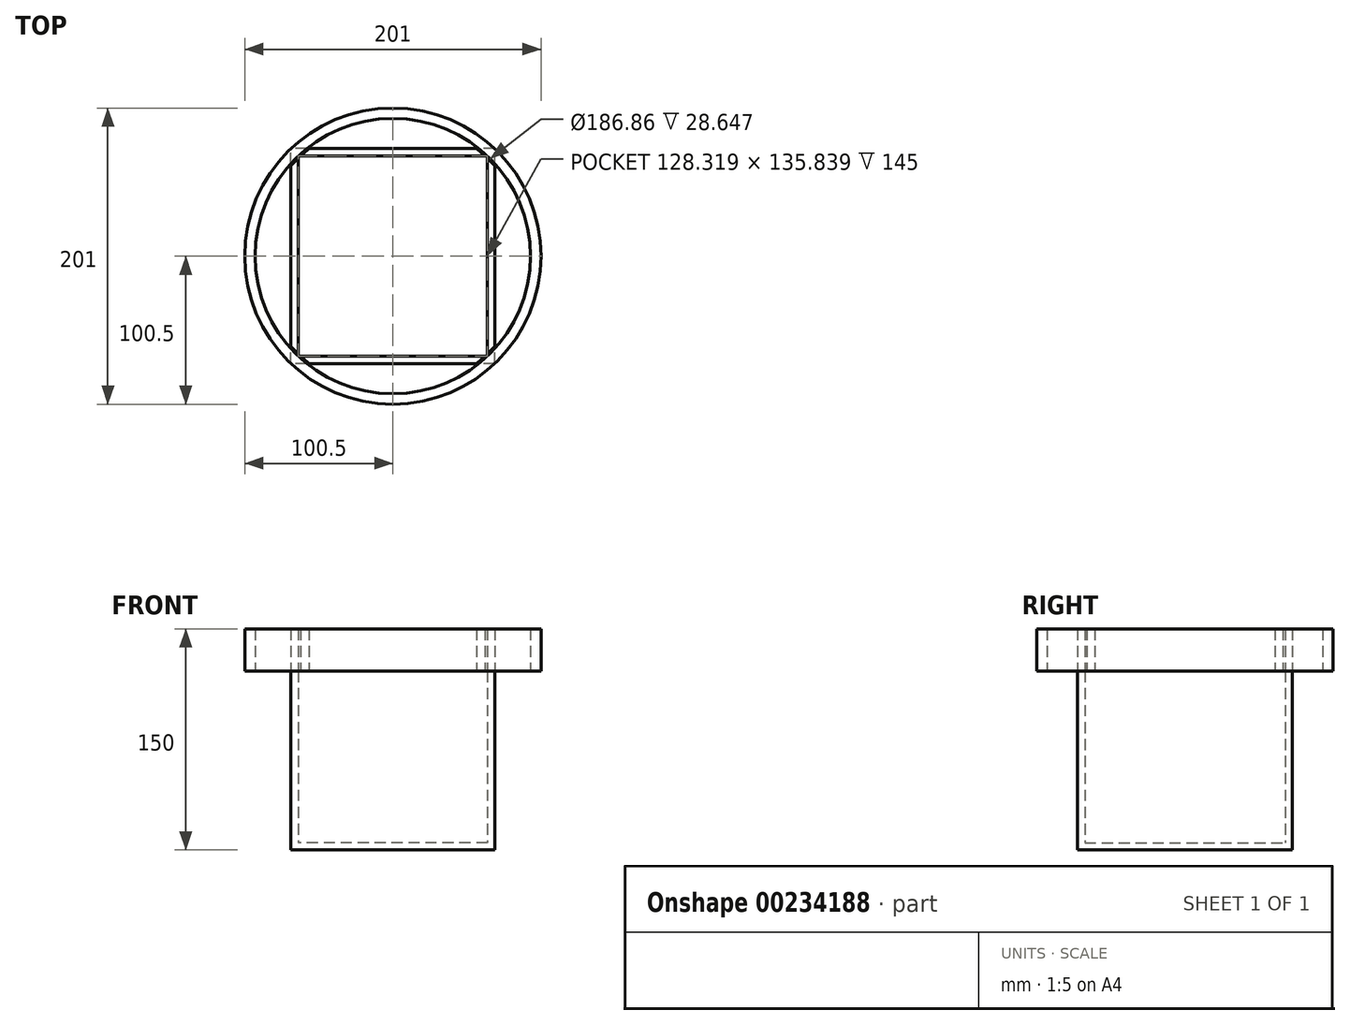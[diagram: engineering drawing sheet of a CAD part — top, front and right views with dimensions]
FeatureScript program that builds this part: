
annotation { "Feature Type Name" : "Feature", "Feature Type Description" : "" }
export const myFeature = defineFeature(function(context is Context, id is Id, definition is map)
    precondition{}
    {
        {
            assignVariable(context, id + "F0", {"name" : "height", "anyValue" : 150});
        }
        {
            assignVariable(context, id + "F1", {"name" : "thickness", "anyValue" : 5});
        }
        {
            assignVariable(context, id + "F2", {"name" : "proportion", "anyValue" : 1 - (1 - 1 / 1.62) / 2});
        }
        {
            var Q0;
            Q0=qCreatedBy(makeId("Top.planeOp"),FACE);
            var sketch = newSketch(context, id + "F3", { "sketchPlane" : qUnion([Q0])});
            skLineSegment(sketch, "E0.bottom", {"start": v(69.16, -72.92) * mm, "end": v(-69.16, -72.92) * mm});
            skLineSegment(sketch, "E0.top", {"start": v(69.16, 72.92) * mm, "end": v(-69.16, 72.92) * mm});
            skLineSegment(sketch, "E0.left", {"start": v(69.16, -72.92) * mm, "end": v(69.16, 72.92) * mm});
            skLineSegment(sketch, "E0.right", {"start": v(-69.16, -72.92) * mm, "end": v(-69.16, 72.92) * mm});
            skPoint(sketch, "E0.middle", {"position": v(0, 0) * mm});
            skCircle(sketch, "E1", {"center": v(0, 0) * mm, "radius": 100.5 * mm, "construction": true});
            skCircle(sketch, "E2", {"center": v(0, 0) * mm, "radius": 93.43 * mm, "construction": true});
            skLineSegment(sketch, "E3.bottom", {"start": v(64.16, -67.92) * mm, "end": v(-64.16, -67.92) * mm});
            skLineSegment(sketch, "E3.top", {"start": v(64.16, 67.92) * mm, "end": v(-64.16, 67.92) * mm});
            skLineSegment(sketch, "E3.left", {"start": v(64.16, -67.92) * mm, "end": v(64.16, 67.92) * mm});
            skLineSegment(sketch, "E3.right", {"start": v(-64.16, -67.92) * mm, "end": v(-64.16, 67.92) * mm});
            skSolve(sketch);
        }
        {
            var Q0;
            Q0=makeQuery(id+"F3.imprint","IMPRINT",FACE,{"disambiguationData":[TD([[makeQuery(id+"F3.imprint","IMPRINT",EDGE,{"derivedFrom":sQuery(id+"F3.wireOp",EDGE,"E3.bottom")}),-1.0]])]});
            extrude(context, id + "F4", {"entities" : qUnion([Q0]), "depth" : getVariable(context, 'thickness') * mm});
        }
        {
            var Q0;
            Q0=makeQuery(id+"F3.imprint","IMPRINT",FACE,{"disambiguationData":[TD([[makeQuery(id+"F3.imprint","IMPRINT",EDGE,{"derivedFrom":sQuery(id+"F3.wireOp",EDGE,"E0.bottom")}),-1.0]])]});
            extrude(context, id + "F5", {"entities" : qUnion([Q0]), "operationType" : NewBodyOperationType.ADD, "depth" : (getVariable(context, 'height') * getVariable(context, 'proportion')) * mm});
        }
        {
            var Q0;
            Q0=makeQuery(id+"F5.opExtrude","CAP_FACE",FACE,{"disambiguationData":[OSD([sQuery(id+"F3.wireOp",EDGE,"E0.bottom"),sQuery(id+"F3.wireOp",EDGE,"E0.top"),sQuery(id+"F3.wireOp",EDGE,"E0.left"),sQuery(id+"F3.wireOp",EDGE,"E0.right"),sQuery(id+"F3.wireOp",EDGE,"E3.bottom"),sQuery(id+"F3.wireOp",EDGE,"E3.top"),sQuery(id+"F3.wireOp",EDGE,"E3.left"),sQuery(id+"F3.wireOp",EDGE,"E3.right")])],"isStart":false});
            var sketch = newSketch(context, id + "F6", { "sketchPlane" : qUnion([Q0])});
            skPoint(sketch, "E4.0", {"position": v(69.16, 72.92) * mm});
            skPoint(sketch, "E5.0", {"position": v(69.16, -72.92) * mm});
            skPoint(sketch, "E6.0", {"position": v(-69.16, -72.92) * mm});
            skPoint(sketch, "E7.0", {"position": v(-69.16, 72.92) * mm});
            skPoint(sketch, "E8.0", {"position": v(-64.16, 67.92) * mm});
            skPoint(sketch, "E9.0", {"position": v(64.16, 67.92) * mm});
            skPoint(sketch, "E10.0", {"position": v(64.16, -67.92) * mm});
            skLineSegment(sketch, "E11", {"start": v(56.76, 72.92) * mm, "end": v(0, 72.92) * mm});
            skLineSegment(sketch, "E12", {"start": v(62.66, 67.92) * mm, "end": v(0, 67.92) * mm});
            skArc(sketch, "E13", {"start": v(56.76, 72.92) * mm, "mid": v(59.76, 70.48) * mm, "end": v(62.66, 67.92) * mm});
            skLineSegment(sketch, "E14.MirrorCS", {"start": v(-62.66, 67.92) * mm, "end": v(0, 67.92) * mm});
            skLineSegment(sketch, "E15.MirrorCS", {"start": v(-56.76, 72.92) * mm, "end": v(0, 72.92) * mm});
            skArc(sketch, "E16.MirrorCS", {"start": v(-56.76, 72.92) * mm, "mid": v(-59.76, 70.48) * mm, "end": v(-62.66, 67.92) * mm});
            skLineSegment(sketch, "E17.MirrorCS", {"start": v(62.66, -67.92) * mm, "end": v(0, -67.92) * mm});
            skArc(sketch, "E18.MirrorCS", {"start": v(56.76, -72.92) * mm, "mid": v(59.76, -70.48) * mm, "end": v(62.66, -67.92) * mm});
            skLineSegment(sketch, "E19.MirrorCS", {"start": v(56.76, -72.92) * mm, "end": v(0, -72.92) * mm});
            skLineSegment(sketch, "E20.MirrorCS", {"start": v(-56.76, -72.92) * mm, "end": v(0, -72.92) * mm});
            skArc(sketch, "E21.MirrorCS", {"start": v(-56.76, -72.92) * mm, "mid": v(-59.76, -70.48) * mm, "end": v(-62.66, -67.92) * mm});
            skLineSegment(sketch, "E22.MirrorCS", {"start": v(-62.66, -67.92) * mm, "end": v(0, -67.92) * mm});
            skLineSegment(sketch, "E23", {"start": v(69.16, 61.2) * mm, "end": v(69.16, 0) * mm});
            skPoint(sketch, "E23.endSnap0", {"position": v(64.16, 0) * mm});
            skArc(sketch, "E24", {"start": v(64.16, 66.42) * mm, "mid": v(66.71, 63.86) * mm, "end": v(69.16, 61.2) * mm});
            skLineSegment(sketch, "E25", {"start": v(64.16, 66.42) * mm, "end": v(64.16, 0) * mm});
            skLineSegment(sketch, "E26.MirrorCS", {"start": v(69.16, -61.2) * mm, "end": v(69.16, 0) * mm});
            skLineSegment(sketch, "E27.MirrorCS", {"start": v(64.16, -66.42) * mm, "end": v(64.16, 0) * mm});
            skArc(sketch, "E28.MirrorCS", {"start": v(64.16, -66.42) * mm, "mid": v(66.71, -63.86) * mm, "end": v(69.16, -61.2) * mm});
            skLineSegment(sketch, "E29.MirrorCS", {"start": v(-64.16, -66.42) * mm, "end": v(-64.16, 0) * mm});
            skLineSegment(sketch, "E30.MirrorCS", {"start": v(-69.16, -61.2) * mm, "end": v(-69.16, 0) * mm});
            skLineSegment(sketch, "E31.MirrorCS", {"start": v(-69.16, 61.2) * mm, "end": v(-69.16, 0) * mm});
            skLineSegment(sketch, "E32.MirrorCS", {"start": v(-64.16, 66.42) * mm, "end": v(-64.16, 0) * mm});
            skArc(sketch, "E33.MirrorCS", {"start": v(-64.16, 66.42) * mm, "mid": v(-66.71, 63.86) * mm, "end": v(-69.16, 61.2) * mm});
            skArc(sketch, "E34.MirrorCS", {"start": v(-64.16, -66.42) * mm, "mid": v(-66.71, -63.86) * mm, "end": v(-69.16, -61.2) * mm});
            skSolve(sketch);
        }
        {
            var Q0;
            Q0=makeQuery(id+"F5.opExtrude","CAP_FACE",FACE,{"disambiguationData":[OSD([sQuery(id+"F3.wireOp",EDGE,"E0.bottom"),sQuery(id+"F3.wireOp",EDGE,"E0.top"),sQuery(id+"F3.wireOp",EDGE,"E0.left"),sQuery(id+"F3.wireOp",EDGE,"E0.right"),sQuery(id+"F3.wireOp",EDGE,"E3.bottom"),sQuery(id+"F3.wireOp",EDGE,"E3.top"),sQuery(id+"F3.wireOp",EDGE,"E3.left"),sQuery(id+"F3.wireOp",EDGE,"E3.right")])],"isStart":false});
            var sketch = newSketch(context, id + "F7", { "sketchPlane" : qUnion([Q0])});
            skCircle(sketch, "E35.0", {"center": v(0, 0) * mm, "radius": 93.43 * mm});
            skCircle(sketch, "E36.0", {"center": v(0, 0) * mm, "radius": 100.5 * mm});
            skPoint(sketch, "E37.0", {"position": v(-69.16, 72.92) * mm});
            skPoint(sketch, "E38.0", {"position": v(69.16, 72.92) * mm});
            skPoint(sketch, "E39.0", {"position": v(69.16, -72.92) * mm});
            skPoint(sketch, "E40.0", {"position": v(-69.16, -72.92) * mm});
            skLineSegment(sketch, "E41", {"start": v(-69.16, 72.92) * mm, "end": v(-69.16, 72.92) * mm});
            skLineSegment(sketch, "E42", {"start": v(-69.16, -72.92) * mm, "end": v(-69.16, -72.92) * mm});
            skLineSegment(sketch, "E43", {"start": v(69.16, -72.92) * mm, "end": v(69.16, -72.92) * mm});
            skLineSegment(sketch, "E44", {"start": v(69.16, 72.92) * mm, "end": v(69.16, 72.92) * mm});
            skLineSegment(sketch, "E45", {"start": v(-69.16, 72.92) * mm, "end": v(69.16, 72.92) * mm, "construction": true});
            skLineSegment(sketch, "E46", {"start": v(-69.16, 72.92) * mm, "end": v(-69.16, -72.92) * mm, "construction": true});
            skLineSegment(sketch, "E47", {"start": v(-69.16, -72.92) * mm, "end": v(69.16, -72.92) * mm, "construction": true});
            skLineSegment(sketch, "E48", {"start": v(69.16, 72.92) * mm, "end": v(69.16, -72.92) * mm, "construction": true});
            skLineSegment(sketch, "E49.bottom", {"start": v(70.16, 73.92) * mm, "end": v(-70.16, 73.92) * mm, "construction": true});
            skLineSegment(sketch, "E49.top", {"start": v(70.16, -73.92) * mm, "end": v(-70.16, -73.92) * mm, "construction": true});
            skLineSegment(sketch, "E49.left", {"start": v(70.16, 73.92) * mm, "end": v(70.16, -73.92) * mm, "construction": true});
            skLineSegment(sketch, "E49.right", {"start": v(-70.16, 73.92) * mm, "end": v(-70.16, -73.92) * mm, "construction": true});
            skSolve(sketch);
        }
        {
            var Q0;
            {var subQ0=sQuery(id+"F7.wireOp",EDGE,"E35.0");var subQ1=makeQuery(id+"F5.opExtrude","CAP_EDGE",EDGE,{"disambiguationData":[OSD([sQuery(id+"F3.wireOp",EDGE,"E0.right")])],"isStart":false});var subQ2=makeQuery(id+"F7.imprint","INTERSECT",VERTEX,{"disambiguationData":[OD(1.0)],"derivedFrom":[subQ1,subQ0]});Q0=makeQuery(id+"F7.imprint","IMPRINT",FACE,{"disambiguationData":[TD([[makeQuery(id+"F7.imprint","IMPRINT",EDGE,{"disambiguationData":[TD([[subQ2,-1.0]])],"derivedFrom":subQ0}),-1.0]])]});}
            var Q1;
            {var subQ0=sQuery(id+"F7.wireOp",EDGE,"E35.0");var subQ1=makeQuery(id+"F5.opExtrude","CAP_EDGE",EDGE,{"disambiguationData":[OSD([sQuery(id+"F3.wireOp",EDGE,"E0.right")])],"isStart":false});var subQ2=makeQuery(id+"F7.imprint","INTERSECT",VERTEX,{"disambiguationData":[OD(0.0)],"derivedFrom":[subQ1,subQ0]});Q1=makeQuery(id+"F7.imprint","IMPRINT",FACE,{"disambiguationData":[TD([[makeQuery(id+"F7.imprint","IMPRINT",EDGE,{"disambiguationData":[TD([[subQ2,-1.0]])],"derivedFrom":subQ0}),-1.0]])]});}
            var Q2;
            {var subQ0=sQuery(id+"F7.wireOp",EDGE,"E35.0");var subQ1=makeQuery(id+"F5.opExtrude","CAP_EDGE",EDGE,{"disambiguationData":[OSD([sQuery(id+"F3.wireOp",EDGE,"E0.top")])],"isStart":false});var subQ2=makeQuery(id+"F7.imprint","INTERSECT",VERTEX,{"disambiguationData":[OD(1.0)],"derivedFrom":[subQ1,subQ0]});Q2=makeQuery(id+"F7.imprint","IMPRINT",FACE,{"disambiguationData":[TD([[makeQuery(id+"F7.imprint","IMPRINT",EDGE,{"disambiguationData":[TD([[subQ2,-1.0]])],"derivedFrom":subQ0}),-1.0]])]});}
            var Q3;
            {var subQ0=sQuery(id+"F7.wireOp",EDGE,"E35.0");var subQ1=makeQuery(id+"F5.opExtrude","CAP_EDGE",EDGE,{"disambiguationData":[OSD([sQuery(id+"F3.wireOp",EDGE,"E0.top")])],"isStart":false});var subQ2=makeQuery(id+"F7.imprint","INTERSECT",VERTEX,{"disambiguationData":[OD(0.0)],"derivedFrom":[subQ1,subQ0]});Q3=makeQuery(id+"F7.imprint","IMPRINT",FACE,{"disambiguationData":[TD([[makeQuery(id+"F7.imprint","IMPRINT",EDGE,{"disambiguationData":[TD([[subQ2,-1.0]])],"derivedFrom":subQ0}),-1.0]])]});}
            var Q4;
            {var subQ0=sQuery(id+"F7.wireOp",EDGE,"E35.0");var subQ1=makeQuery(id+"F5.opExtrude","CAP_EDGE",EDGE,{"disambiguationData":[OSD([sQuery(id+"F3.wireOp",EDGE,"E0.top")])],"isStart":false});var subQ2=makeQuery(id+"F7.imprint","INTERSECT",VERTEX,{"disambiguationData":[OD(0.0)],"derivedFrom":[subQ1,subQ0]});Q4=makeQuery(id+"F7.imprint","IMPRINT",FACE,{"disambiguationData":[TD([[makeQuery(id+"F7.imprint","IMPRINT",EDGE,{"disambiguationData":[TD([[subQ2,1.0]])],"derivedFrom":subQ0}),-1.0]])]});}
            var Q5;
            {var subQ0=sQuery(id+"F7.wireOp",EDGE,"E35.0");var subQ1=makeQuery(id+"F5.opExtrude","CAP_EDGE",EDGE,{"disambiguationData":[OSD([sQuery(id+"F3.wireOp",EDGE,"E0.left")])],"isStart":false});var subQ2=makeQuery(id+"F7.imprint","INTERSECT",VERTEX,{"disambiguationData":[OD(0.0)],"derivedFrom":[subQ1,subQ0]});Q5=makeQuery(id+"F7.imprint","IMPRINT",FACE,{"disambiguationData":[TD([[makeQuery(id+"F7.imprint","IMPRINT",EDGE,{"disambiguationData":[TD([[subQ2,1.0]])],"derivedFrom":subQ0}),-1.0]])]});}
            var Q6;
            {var subQ0=sQuery(id+"F7.wireOp",EDGE,"E35.0");var subQ1=makeQuery(id+"F5.opExtrude","CAP_EDGE",EDGE,{"disambiguationData":[OSD([sQuery(id+"F3.wireOp",EDGE,"E0.bottom")])],"isStart":false});var subQ2=makeQuery(id+"F7.imprint","INTERSECT",VERTEX,{"disambiguationData":[OD(1.0)],"derivedFrom":[subQ1,subQ0]});Q6=makeQuery(id+"F7.imprint","IMPRINT",FACE,{"disambiguationData":[TD([[makeQuery(id+"F7.imprint","IMPRINT",EDGE,{"disambiguationData":[TD([[subQ2,-1.0]])],"derivedFrom":subQ0}),-1.0]])]});}
            var Q7;
            {var subQ0=sQuery(id+"F7.wireOp",EDGE,"E35.0");var subQ1=makeQuery(id+"F5.opExtrude","CAP_EDGE",EDGE,{"disambiguationData":[OSD([sQuery(id+"F3.wireOp",EDGE,"E0.bottom")])],"isStart":false});var subQ2=makeQuery(id+"F7.imprint","INTERSECT",VERTEX,{"disambiguationData":[OD(0.0)],"derivedFrom":[subQ1,subQ0]});Q7=makeQuery(id+"F7.imprint","IMPRINT",FACE,{"disambiguationData":[TD([[makeQuery(id+"F7.imprint","IMPRINT",EDGE,{"disambiguationData":[TD([[subQ2,-1.0]])],"derivedFrom":subQ0}),-1.0]])]});}
            extrude(context, id + "F8", {"entities" : qUnion([Q0, Q1, Q2, Q3, Q4, Q5, Q6, Q7]), "depth" : (getVariable(context, 'height') * (1 - getVariable(context, 'proportion'))) * mm});
        }
        {
            var Q0;
            Q0=makeQuery(id+"F6.imprint","IMPRINT",FACE,{"disambiguationData":[TD([[makeQuery(id+"F6.imprint","IMPRINT",EDGE,{"derivedFrom":sQuery(id+"F6.wireOp",EDGE,"E23")}),1.0]])]});
            var Q1;
            Q1=makeQuery(id+"F6.imprint","IMPRINT",FACE,{"disambiguationData":[TD([[makeQuery(id+"F6.imprint","IMPRINT",EDGE,{"derivedFrom":sQuery(id+"F6.wireOp",EDGE,"E11")}),1.0]])]});
            var Q2;
            Q2=makeQuery(id+"F6.imprint","IMPRINT",FACE,{"disambiguationData":[TD([[makeQuery(id+"F6.imprint","IMPRINT",EDGE,{"derivedFrom":sQuery(id+"F6.wireOp",EDGE,"E29.MirrorCS")}),1.0]])]});
            var Q3;
            Q3=makeQuery(id+"F6.imprint","IMPRINT",FACE,{"disambiguationData":[TD([[makeQuery(id+"F6.imprint","IMPRINT",EDGE,{"derivedFrom":sQuery(id+"F6.wireOp",EDGE,"E17.MirrorCS")}),1.0]])]});
            extrude(context, id + "F9", {"entities" : qUnion([Q0, Q1, Q2, Q3]), "operationType" : NewBodyOperationType.ADD, "depth" : (getVariable(context, 'height') * (1 - getVariable(context, 'proportion'))) * mm});
        }
    });
